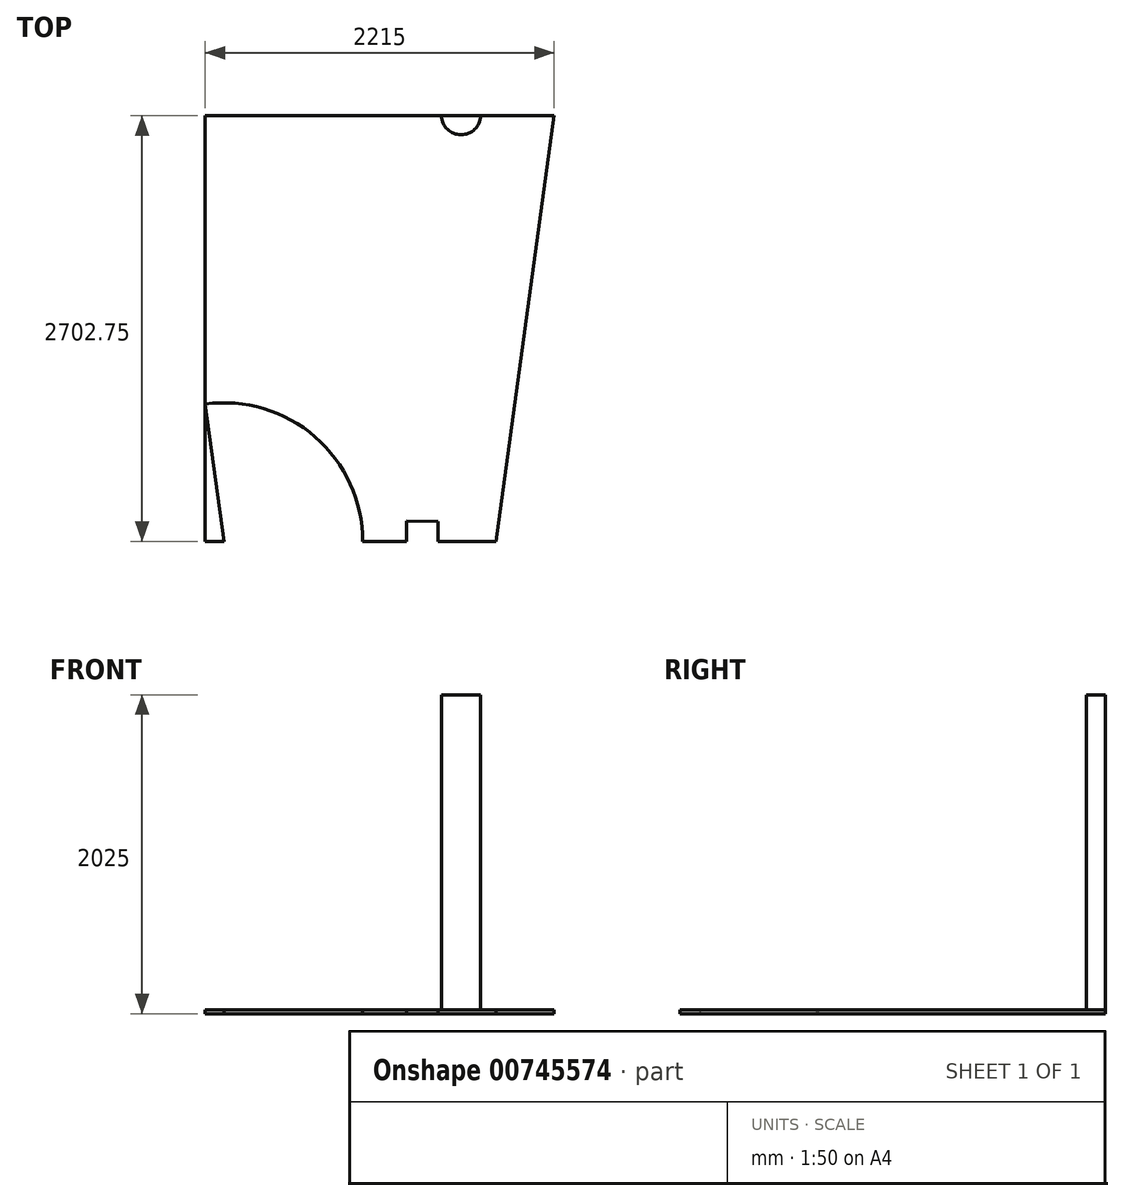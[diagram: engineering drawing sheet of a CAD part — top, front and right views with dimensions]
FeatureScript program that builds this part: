
annotation { "Feature Type Name" : "Feature", "Feature Type Description" : "" }
export const myFeature = defineFeature(function(context is Context, id is Id, definition is map)
    precondition{}
    {
        {
            var Q0;
            Q0=qCreatedBy(makeId("Top.planeOp"),FACE);
            var sketch = newSketch(context, id + "F0", { "sketchPlane" : qUnion([Q0])});
            skLineSegment(sketch, "E0", {"start": v(-1128.7, -1019.14) * mm, "end": v(-1128.7, 1545.86) * mm});
            skLineSegment(sketch, "E1", {"start": v(-1128.7, 1545.86) * mm, "end": v(1086.3, 1545.86) * mm});
            skLineSegment(sketch, "E2", {"start": v(1086.3, 1545.86) * mm, "end": v(736.26, -1032.84) * mm});
            skLineSegment(sketch, "E3", {"start": v(736.26, -1032.84) * mm, "end": v(-1128.7, -1019.14) * mm});
            skLineSegment(sketch, "E4", {"start": v(-1128.7, -1019.14) * mm, "end": v(-1128.7, -1156.89) * mm});
            skLineSegment(sketch, "E5", {"start": v(-1128.7, -1156.89) * mm, "end": v(151.3, -1156.89) * mm});
            skLineSegment(sketch, "E6", {"start": v(151.3, -1156.89) * mm, "end": v(151.3, -1028.54) * mm});
            skLineSegment(sketch, "E7", {"start": v(351.3, -1030.01) * mm, "end": v(351.3, -1156.89) * mm});
            skLineSegment(sketch, "E8", {"start": v(736.26, -1032.84) * mm, "end": v(719.42, -1156.89) * mm});
            skLineSegment(sketch, "E9", {"start": v(351.3, -1156.89) * mm, "end": v(719.42, -1156.89) * mm});
            skPoint(sketch, "E10.orphan", {"position": v(151.3, -1019.14) * mm});
            skSolve(sketch);
        }
        {
            var Q0;
            {var subQ3=sQuery(id+"F0.wireOp",EDGE,"E0");Q0=makeQuery(id+"F0.imprint","IMPRINT",FACE,{"disambiguationData":[TD([[makeQuery(id+"F0.imprint","IMPRINT",EDGE,{"derivedFrom":subQ3}),-1.0]])]});}
            var Q1;
            {var subQ0=sQuery(id+"F0.wireOp",EDGE,"E4");Q1=makeQuery(id+"F0.imprint","IMPRINT",FACE,{"disambiguationData":[TD([[makeQuery(id+"F0.imprint","IMPRINT",EDGE,{"derivedFrom":subQ0}),1.0]])]});}
            var Q2;
            {var subQ2=sQuery(id+"F0.wireOp",EDGE,"E7");Q2=makeQuery(id+"F0.imprint","IMPRINT",FACE,{"disambiguationData":[TD([[makeQuery(id+"F0.imprint","IMPRINT",EDGE,{"derivedFrom":subQ2}),1.0]])]});}
            extrude(context, id + "F1", {"entities" : qUnion([Q0, Q1, Q2]), "depth" : 25 * mm, "offsetDistance" : 25 * mm});
        }
        {
            var Q0;
            Q0=makeQuery(id+"F1.opExtrude","CAP_FACE",FACE,{"disambiguationData":[OSD([sQuery(id+"F0.wireOp",EDGE,"E0"),sQuery(id+"F0.wireOp",EDGE,"E1"),sQuery(id+"F0.wireOp",EDGE,"E2"),sQuery(id+"F0.wireOp",EDGE,"E3"),sQuery(id+"F0.wireOp",EDGE,"E4"),sQuery(id+"F0.wireOp",EDGE,"E5"),sQuery(id+"F0.wireOp",EDGE,"E6"),sQuery(id+"F0.wireOp",EDGE,"E7"),sQuery(id+"F0.wireOp",EDGE,"E8"),sQuery(id+"F0.wireOp",EDGE,"E9")])],"isStart":false});
            var sketch = newSketch(context, id + "F2", { "sketchPlane" : qUnion([Q0])});
            skLineSegment(sketch, "E11", {"start": v(-1128.7, -1156.89) * mm, "end": v(-1008.7, -1156.89) * mm});
            skLineSegment(sketch, "E12", {"start": v(-1008.7, -1156.89) * mm, "end": v(-1008.7, -276.89) * mm});
            skArc(sketch, "E13", {"start": v(-128.7, -1156.89) * mm, "mid": v(-386.44, -534.63) * mm, "end": v(-1008.7, -276.89) * mm});
            skArc(sketch, "E14", {"start": v(-1008.7, -276.89) * mm, "mid": v(-1477.97, -412.46) * mm, "end": v(-1802.66, -777.4) * mm});
            skLineSegment(sketch, "E15", {"start": v(-1008.7, -1156.89) * mm, "end": v(-1128.7, -285.1) * mm});
            skSolve(sketch);
        }
        {
            var Q0;
            {var subQ0=sQuery(id+"F2.wireOp",EDGE,"E12");Q0=makeQuery(id+"F2.imprint","IMPRINT",FACE,{"disambiguationData":[TD([[makeQuery(id+"F2.imprint","IMPRINT",EDGE,{"derivedFrom":subQ0}),-1.0]])]});}
            var Q1;
            {var subQ0=sQuery(id+"F2.wireOp",EDGE,"E12");Q1=makeQuery(id+"F2.imprint","IMPRINT",FACE,{"disambiguationData":[TD([[makeQuery(id+"F2.imprint","IMPRINT",EDGE,{"derivedFrom":subQ0}),1.0]])]});}
            extrude(context, id + "F3", {"entities" : qUnion([Q0, Q1]), "operationType" : NewBodyOperationType.REMOVE, "endBound" : BoundingType.THROUGH_ALL, "oppositeDirection" : true, "depth" : 25 * mm, "offsetDistance" : 25 * mm});
        }
        {
            var Q0;
            {var subQ0=sQuery(id+"F0.wireOp",EDGE,"E3");var subQ1=sQuery(id+"F0.wireOp",EDGE,"E8");var subQ2=sQuery(id+"F0.wireOp",EDGE,"E2");var subQ3=sQuery(id+"F0.wireOp",EDGE,"E1");var subQ4=sQuery(id+"F0.wireOp",EDGE,"E4");var subQ5=sQuery(id+"F0.wireOp",EDGE,"E0");var subQ6=sQuery(id+"F0.wireOp",EDGE,"E5");var subQ7=sQuery(id+"F0.wireOp",EDGE,"E6");var subQ8=sQuery(id+"F0.wireOp",EDGE,"E7");var subQ9=sQuery(id+"F0.wireOp",EDGE,"E9");Q0=makeQuery(id+"F3.boolean.opBoolean","SPLIT",FACE,{"disambiguationData":[TD([makeQuery(id+"F1.opExtrude","SWEPT_FACE",FACE,{"disambiguationData":[OSD([subQ3])]})])],"derivedFrom":makeQuery(id+"F1.opExtrude","CAP_FACE",FACE,{"disambiguationData":[OSD([subQ5,subQ3,subQ2,subQ0,subQ4,subQ6,subQ7,subQ8,subQ1,subQ9])],"isStart":false})});}
            var sketch = newSketch(context, id + "F4", { "sketchPlane" : qUnion([Q0])});
            skLineSegment(sketch, "E16.bottom", {"start": v(371.3, 1545.86) * mm, "end": v(621.3, 1545.86) * mm});
            skLineSegment(sketch, "E16.top", {"start": v(371.3, 1425.86) * mm, "end": v(621.3, 1425.86) * mm});
            skLineSegment(sketch, "E16.left", {"start": v(371.3, 1545.86) * mm, "end": v(371.3, 1425.86) * mm});
            skLineSegment(sketch, "E16.right", {"start": v(621.3, 1545.86) * mm, "end": v(621.3, 1425.86) * mm});
            skCircle(sketch, "E17", {"center": v(496.3, 1550.97) * mm, "radius": 125.1 * mm});
            skPoint(sketch, "E17.third.point", {"position": v(496.3, 1425.86) * mm});
            skSolve(sketch);
        }
        {
            var Q0;
            {var subQ0=sQuery(id+"F4.wireOp",EDGE,"E16.bottom");Q0=makeQuery(id+"F4.imprint","IMPRINT",FACE,{"disambiguationData":[TD([[makeQuery(id+"F4.imprint","IMPRINT",EDGE,{"derivedFrom":subQ0}),-1.0]])]});}
            extrude(context, id + "F5", {"entities" : qUnion([Q0]), "operationType" : NewBodyOperationType.ADD, "depth" : 2000 * mm, "offsetDistance" : 25 * mm});
        }
    });
